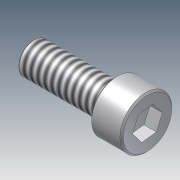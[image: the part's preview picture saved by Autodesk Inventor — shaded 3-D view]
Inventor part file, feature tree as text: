
AUTODESK INVENTOR PART (.ipt)
format: ipt  version: 2012 (Build 160160000, 160)  size: 114,688 bytes
history: native  units: in
note: dims shown in document units (in); Inventor stores cm internally (conversion verified against a paired STEP export)
features: sketch x2, revolve x1, thread x1, extrude x1, chamfer x1
ambient origin geometry x8: Origin, YZ Plane, XZ Plane, XY Plane, X Axis, Y Axis, Z Axis, Center Point
bodies: Solid1 (feature_tree)
feature tree (6):
  revolve  "Revolution1"  [1 undecoded]
  thread  "Thread1"  [1 undecoded]
  extrude  "Extrusion1"  TaperAngle=90.0deg  [1 undecoded]
  chamfer  "Chamfer1"  Distance=1.0in
  sketch  "Sketch1"  dims[d0=0.5in d1=0.094in d2=0.19in]
  sketch  "Sketch2"  dims[d3=0.156in d4=90.0deg d5=1.0in d6=0.0in d18=0.1562in d19=0.075in d20=0.0in d21=0.01in d22=0.125in d23=45.0deg d7=1.0in d8=1.0in]
note: 3 required parameter values undecoded (feature->parameter linkage not recoverable at this tier; creation-order binding heuristic only, values carry confidence <= 0.55)